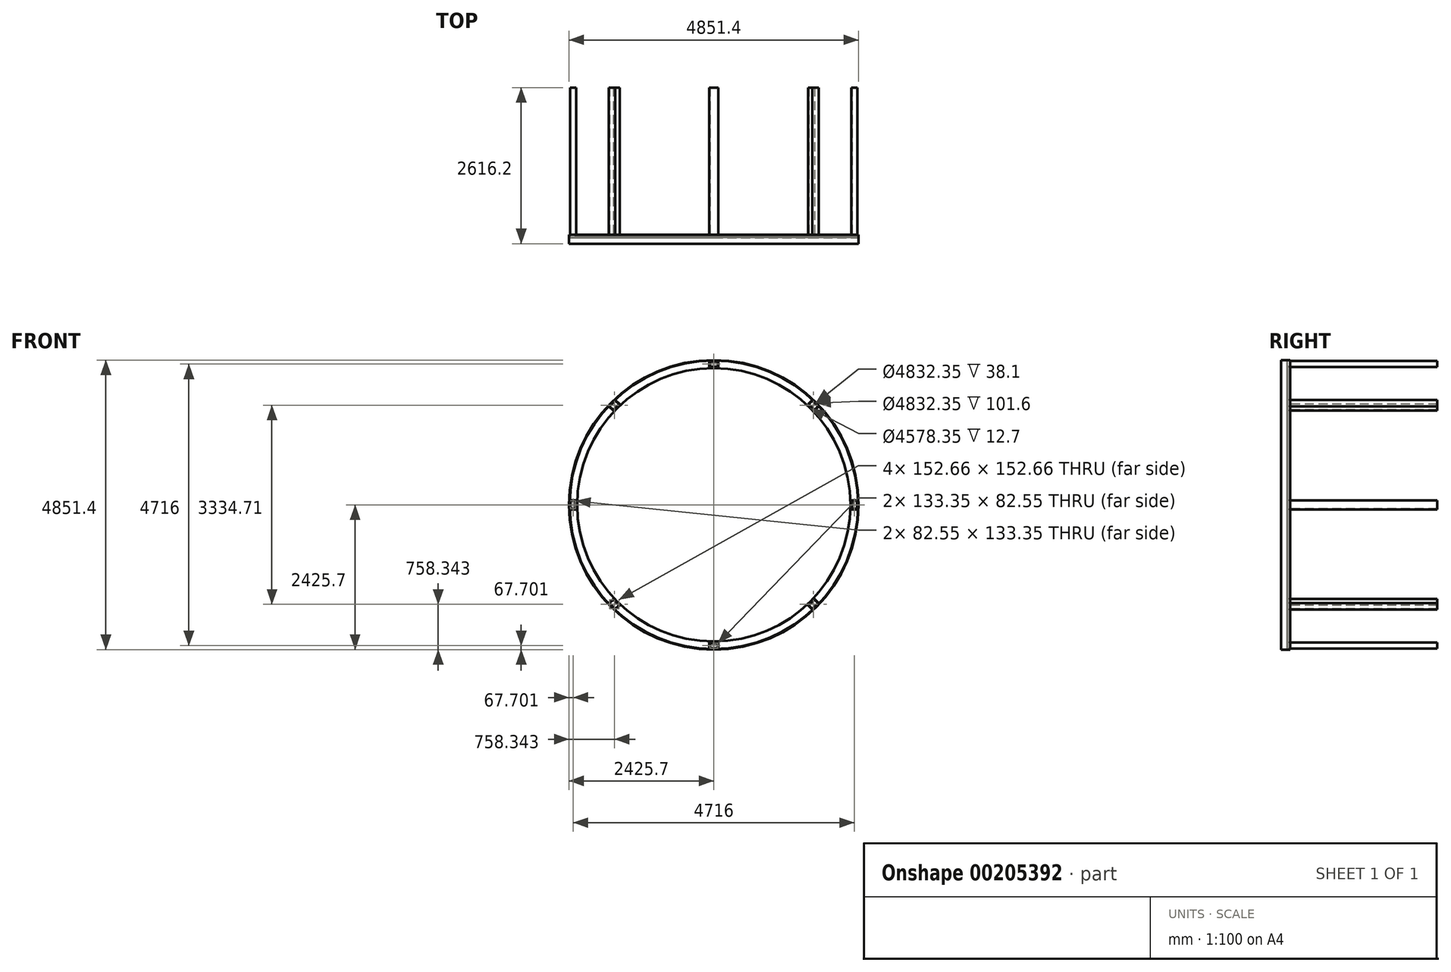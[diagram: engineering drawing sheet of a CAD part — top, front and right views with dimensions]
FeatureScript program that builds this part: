
annotation { "Feature Type Name" : "Feature", "Feature Type Description" : "" }
export const myFeature = defineFeature(function(context is Context, id is Id, definition is map)
    precondition{}
    {
        {
            var Q0;
            Q0=qCreatedBy(makeId("Front.planeOp"),FACE);
            var sketch = newSketch(context, id + "F0", { "sketchPlane" : qUnion([Q0])});
            skCircle(sketch, "E0", {"center": v(0, 0) * mm, "radius": 2416.18 * mm});
            skCircle(sketch, "E1.0", {"center": v(0, 0) * mm, "radius": 2425.7 * mm});
            skSolve(sketch);
        }
        {
            var Q0;
            Q0 = qSketchRegion(id + "F0", true);
            extrude(context, id + "F1", {"entities" : qUnion([Q0]), "depth" : 152.4 * mm});
        }
        {
            var Q0;
            Q0=qCreatedBy(makeId("Front.planeOp"),FACE);
            cPlane(context, id + "F2", {"entities" : qUnion([Q0]), "cplaneType" : CPlaneType.OFFSET, "offset" : 38.1 * mm, "width" : 152.4 * mm, "height" : 152.4 * mm});
        }
        {
            var Q0;
            Q0=qCreatedBy(id+"F2.planeOp",FACE);
            var sketch = newSketch(context, id + "F3", { "sketchPlane" : qUnion([Q0])});
            skCircle(sketch, "E2", {"center": v(0, 0) * mm, "radius": 2416.18 * mm});
            skCircle(sketch, "E3", {"center": v(0, 0) * mm, "radius": 2289.18 * mm});
            skSolve(sketch);
        }
        {
            var Q0;
            Q0 = qSketchRegion(id + "F3", true);
            extrude(context, id + "F4", {"entities" : qUnion([Q0]), "operationType" : NewBodyOperationType.ADD, "depth" : 12.7 * mm});
        }
        {
            var Q0;
            Q0=makeQuery(id+"F4.opExtrude","CAP_FACE",FACE,{"disambiguationData":[OSD([sQuery(id+"F3.wireOp",EDGE,"E2"),sQuery(id+"F3.wireOp",EDGE,"E3")])],"isStart":false});
            var sketch = newSketch(context, id + "F5", { "sketchPlane" : qUnion([Q0])});
            skLineSegment(sketch, "E4", {"start": v(-2408.8, 0) * mm, "end": v(-2408.8, 76.2) * mm});
            skLineSegment(sketch, "E5", {"start": v(-2408.8, 76.2) * mm, "end": v(-2307.2, 76.2) * mm});
            skLineSegment(sketch, "E6", {"start": v(-2307.2, 76.2) * mm, "end": v(-2307.2, -76.2) * mm});
            skLineSegment(sketch, "E7", {"start": v(-2307.2, -76.2) * mm, "end": v(-2408.8, -76.2) * mm});
            skLineSegment(sketch, "E8", {"start": v(-2408.8, -76.2) * mm, "end": v(-2408.8, 0) * mm});
            skLineSegment(sketch, "E9.0", {"start": v(-2316.72, 66.67) * mm, "end": v(-2316.72, -66.68) * mm});
            skLineSegment(sketch, "E9.1", {"start": v(-2399.27, 66.67) * mm, "end": v(-2316.72, 66.67) * mm});
            skLineSegment(sketch, "E9.2", {"start": v(-2316.72, -66.68) * mm, "end": v(-2399.27, -66.68) * mm});
            skLineSegment(sketch, "E9.3", {"start": v(-2399.27, -66.68) * mm, "end": v(-2399.27, 0) * mm});
            skLineSegment(sketch, "E9.4", {"start": v(-2399.27, 0) * mm, "end": v(-2399.27, 66.67) * mm});
            skSolve(sketch);
        }
        {
            var Q0;
            Q0=makeQuery(id+"F5.imprint","IMPRINT",FACE,{"disambiguationData":[TD([[makeQuery(id+"F5.imprint","IMPRINT",EDGE,{"derivedFrom":sQuery(id+"F5.wireOp",EDGE,"E4")}),-1.0]])]});
            extrude(context, id + "F6", {"entities" : qUnion([Q0]), "oppositeDirection" : true, "depth" : 2514.6 * mm});
        }
        {
            var Q0;
            Q0=makeQuery(id+"F6.opExtrude","SWEPT_BODY",BODY,{"disambiguationData":[OSD([sQuery(id+"F5.wireOp",EDGE,"E4"),sQuery(id+"F5.wireOp",EDGE,"E5"),sQuery(id+"F5.wireOp",EDGE,"E6"),sQuery(id+"F5.wireOp",EDGE,"E7"),sQuery(id+"F5.wireOp",EDGE,"E8"),sQuery(id+"F5.wireOp",EDGE,"E9.0"),sQuery(id+"F5.wireOp",EDGE,"E9.1"),sQuery(id+"F5.wireOp",EDGE,"E9.2"),sQuery(id+"F5.wireOp",EDGE,"E9.3"),sQuery(id+"F5.wireOp",EDGE,"E9.4")])]});
            var Q1;
            Q1=makeQuery(id+"F4.opExtrude","CAP_EDGE",EDGE,{"disambiguationData":[OSD([sQuery(id+"F3.wireOp",EDGE,"E3")])],"isStart":true});
            circularPattern(context, id + "F7", {"entities" : qUnion([Q0]), "axis" : qUnion([Q1]), "angle" : 360 * degree, "instanceCount" : 8, "equalSpace" : true, "computeTransformsWithoutBuiltin" : true});
        }
    });
